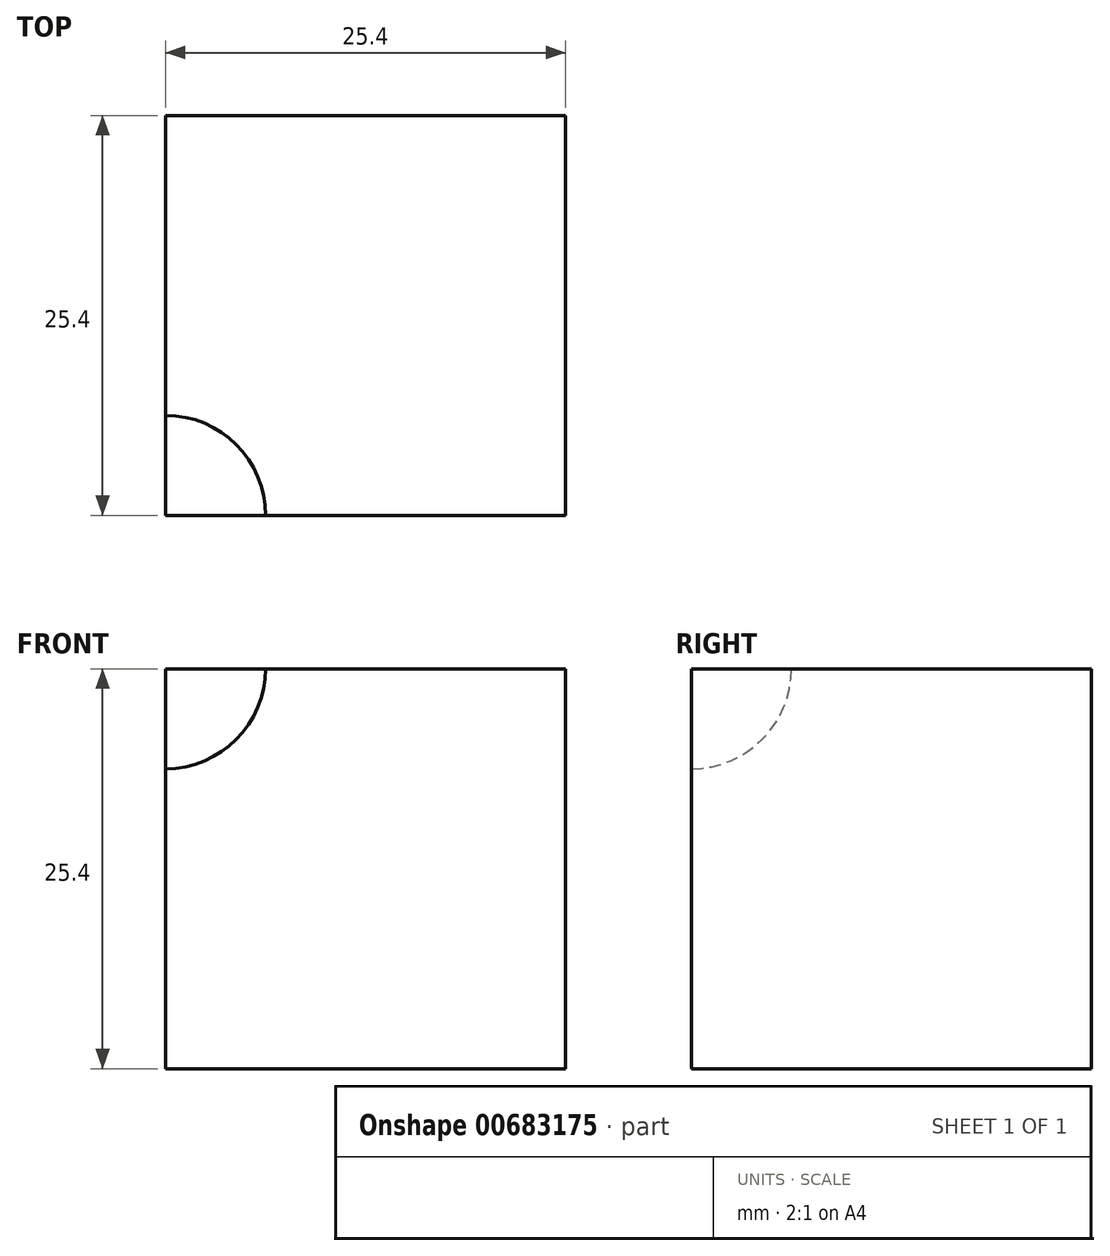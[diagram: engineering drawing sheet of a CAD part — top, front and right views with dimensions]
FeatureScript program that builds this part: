
annotation { "Feature Type Name" : "Feature", "Feature Type Description" : "" }
export const myFeature = defineFeature(function(context is Context, id is Id, definition is map)
    precondition{}
    {
        {
            var Q0;
            Q0=qCreatedBy(makeId("Top.planeOp"),FACE);
            var sketch = newSketch(context, id + "F0", { "sketchPlane" : qUnion([Q0])});
            skLineSegment(sketch, "E0.bottom", {"start": v(0, 0) * mm, "end": v(25.4, 0) * mm});
            skLineSegment(sketch, "E0.top", {"start": v(0, -25.4) * mm, "end": v(25.4, -25.4) * mm});
            skLineSegment(sketch, "E0.left", {"start": v(0, 0) * mm, "end": v(0, -25.4) * mm});
            skLineSegment(sketch, "E0.right", {"start": v(25.4, 0) * mm, "end": v(25.4, -25.4) * mm});
            skSolve(sketch);
        }
        {
            var Q0;
            Q0=makeQuery(id+"F0.imprint","IMPRINT",FACE,{"disambiguationData":[TD([[makeQuery(id+"F0.imprint","IMPRINT",EDGE,{"derivedFrom":sQuery(id+"F0.wireOp",EDGE,"E0.bottom")}),-1.0]])]});
            extrude(context, id + "F1", {"entities" : qUnion([Q0]), "depth" : 25.4 * mm, "offsetDistance" : 25.4 * mm});
        }
        {
            var Q0;
            Q0=makeQuery(id+"F1.opExtrude","CAP_FACE",FACE,{"disambiguationData":[OSD([sQuery(id+"F0.wireOp",EDGE,"E0.bottom"),sQuery(id+"F0.wireOp",EDGE,"E0.top"),sQuery(id+"F0.wireOp",EDGE,"E0.left"),sQuery(id+"F0.wireOp",EDGE,"E0.right")])],"isStart":false});
            var sketch = newSketch(context, id + "F2", { "sketchPlane" : qUnion([Q0])});
            skArc(sketch, "E1", {"start": v(6.35, -25.4) * mm, "mid": v(0, -19.05) * mm, "end": v(-6.35, -25.4) * mm});
            skLineSegment(sketch, "E2", {"start": v(-6.35, -25.4) * mm, "end": v(6.35, -25.4) * mm});
            skSolve(sketch);
        }
        {
            var Q0;
            Q0 = qSketchRegion(id + "F2", true);
            var Q1;
            Q1=sQuery(id+"F2.wireOp",EDGE,"E2");
            revolve(context, id + "F3", {"operationType" : NewBodyOperationType.ADD, "entities" : qUnion([Q0]), "axis" : qUnion([Q1]), "revolveType" : RevolveType.FULL});
        }
    });
